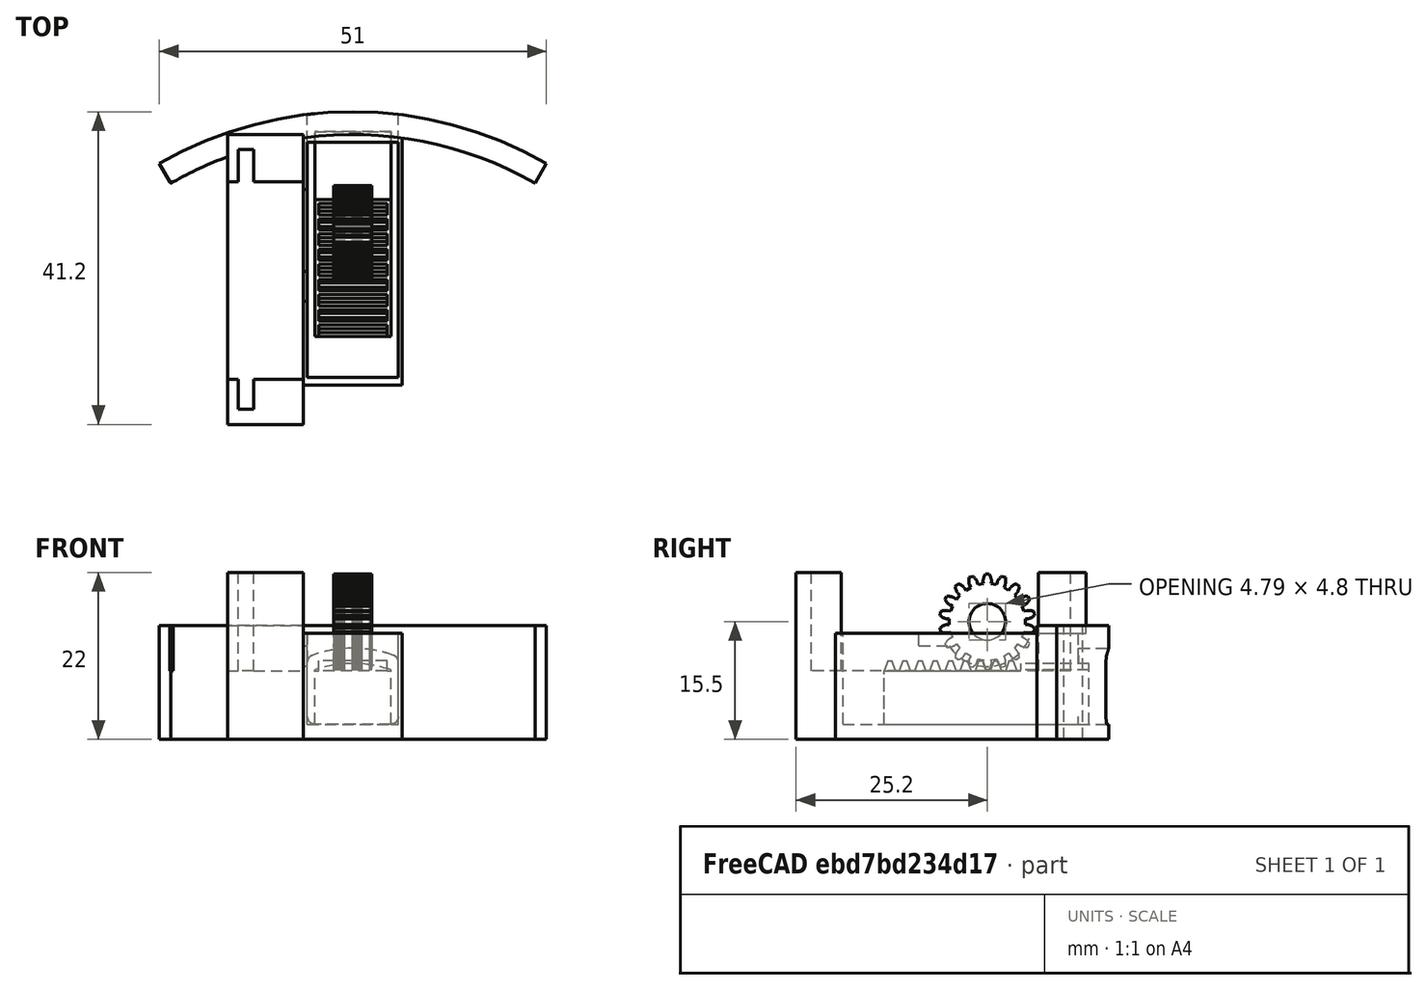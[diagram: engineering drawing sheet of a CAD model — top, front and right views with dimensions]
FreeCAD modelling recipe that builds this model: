
FCSTD DOCUMENT  (FreeCAD 0.16R4924 (Git))
Label: interior_servo_bay_v4p14
License: All rights reserved
LicenseURL: http://en.wikipedia.org/wiki/All_rights_reserved
objects: Part::Feature×11, Part::Box×10, Part::MultiFuse×7, Part::Cut×6, Part::Cylinder×4, Part::Extrusion×3, Part::Thickness×1, Mesh::Feature×1, Part::Fuse×1, Part::FeaturePython×1, Part::Prism×1, Part::MultiCommon×1
note: 46 computed .brp shape members not serialized (recipe doc carries the construction recipe); baked Part::Feature solids carry a one-line shape summary decoded from their .brp

FEATURE [Part::Cylinder] Cylinder  label="bottle_wall"
  Angle = 60
  Height = 15
  Placement = pos=(8.5,-7,0) rot=(0,0,1;1.0472rad)
  Radius = 51
FEATURE [Part::Cylinder] Cylinder001  label="bottle_wall001"
  Angle = 60
  Height = 15
  Placement = pos=(8.5,-7,0) rot=(0,0,1;1.0472rad)
  Radius = 48
FEATURE [Part::Cut] Cut  label="bottle_wall_composite"
  Base = -> Cylinder
  Placement = pos=(0,-2,0) rot=(0,0,1;0rad)
  Tool = -> Cylinder001
FEATURE [Part::Feature] Common_cs  label="pin_cs"
  Placement = pos=(3.5,35,2) rot=(0,0,1;0rad)
  shape: bbox 10 x 2e-07 x 8 mm, 0 faces, 0 solids (baked)
FEATURE [Part::Extrusion] Extrude
  Base = -> Common_cs
  Dir = (0,5,0)
  Solid = true
FEATURE [Part::Thickness] Thickness
  Faces = -> Extrude [Face7]
  Intersection = false
  Join = 0
  Mode = 0
  SelfIntersection = false
  Value = 1
FEATURE [Part::Feature] Common_cs001  label="pin_cs001"
  Placement = pos=(3.5,35,2) rot=(0,0,1;0rad)
  shape: bbox 10 x 2e-07 x 8 mm, 0 faces, 0 solids (baked)
FEATURE [Part::Extrusion] Extrude001
  Base = -> Common_cs001
  Dir = (0,5,0)
  Solid = true
FEATURE [Part::MultiFuse] Fusion  label="bolt_bottle_side_opening"
  Placement = pos=(0,-7,1) rot=(0,0,1;0rad)
  Shapes = -> [Thickness,Extrude,Extrude001]
FEATURE [Part::Box] Box  label="pullBay"
  Height = 15
  Length = 12
  Placement = pos=(2.5,7,2) rot=(0,0,1;0rad)
  Width = 31
FEATURE [Part::Box] Box001  label="Case"
  Height = 14
  Length = 13
  Placement = pos=(2,6,0) rot=(0,0,1;0rad)
  Width = 34
FEATURE [Part::Cut] Cut001  label="cut bay from case"
  Base = -> Box001
  Tool = -> Box
FEATURE [Part::MultiFuse] Fusion001  label="wall plus case"
  Shapes = -> [Cut,Cut001]
FEATURE [Part::Cut] Cut002  label="hole cut out of case"
  Base = -> Fusion001
  Tool = -> Fusion
FEATURE [Mesh::Feature] Mesh  label="servo_motor_2"
  Placement = pos=(33.6,-52,22) rot=(0,0,-1;1.5708rad)
FEATURE [Part::Fuse] union  label="pinion"
FEATURE [Part::FeaturePython] RefineLinearExtrude  # WARN: FeaturePython — macro-defined, semantics opaque (R4)
  Base = -> union
FEATURE [Part::Extrusion] LinearExtrude
  Base = -> RefineLinearExtrude
  Dir = (0,0,5)
  Solid = true
FEATURE [Part::Prism] prism
  Circumradius = 2.4
  Height = 7
  Placement = pos=(0,0,-1) rot=(0,0,1;0rad)
  Polygon = 50
FEATURE [Part::Cut] difference  label="pinion_final"
  Base = -> LinearExtrude
  Placement = pos=(6,26,15.5) rot=(0,1,0;1.5708rad)
  Tool = -> prism
FEATURE [Part::Cylinder] Cylinder002  label="rounded_top"
  Angle = 360
  Height = 40
  Placement = pos=(5,35,-7) rot=(1,0,0;1.5708rad)
  Radius = 15
FEATURE [Part::Box] Box005  label="pin"
  Height = 8
  Length = 10
  Width = 27
FEATURE [Part::MultiCommon] Common  label="rounded pin"
  Shapes = -> [Cylinder002,Box005]
FEATURE [Part::Box] Box006  label="flat_top"
  Height = 10
  Length = 10
  Placement = pos=(0,0,7) rot=(0,0,1;0rad)
  Width = 18
FEATURE [Part::Cut] Cut005
  Base = -> Common
  Placement = pos=(0,11,0) rot=(0,0,1;0rad)
  Tool = -> Box006
FEATURE [Part::Box] cube
  Height = 5
  Length = 18
  Placement = pos=(-12,-4.5,-2.5) rot=(0,0,1;0rad)
  Width = 9
FEATURE [Part::Feature] polyhedron
  Placement = pos=(-11.2451,0,2.5) rot=(0,0,1;0rad)
  shape: bbox 1.51 x 9 x 1.337 mm, 6 faces (baked)
FEATURE [Part::Feature] polyhedron001
  Placement = pos=(-9.24512,0,2.5) rot=(0,0,1;0rad)
  shape: bbox 1.51 x 9 x 1.337 mm, 6 faces (baked)
FEATURE [Part::Feature] polyhedron002
  Placement = pos=(-7.24512,0,2.5) rot=(0,0,1;0rad)
  shape: bbox 1.51 x 9 x 1.337 mm, 6 faces (baked)
FEATURE [Part::Feature] polyhedron003
  Placement = pos=(-5.24512,0,2.5) rot=(0,0,1;0rad)
  shape: bbox 1.51 x 9 x 1.337 mm, 6 faces (baked)
FEATURE [Part::Feature] polyhedron004
  Placement = pos=(-3.24512,0,2.5) rot=(0,0,1;0rad)
  shape: bbox 1.51 x 9 x 1.337 mm, 6 faces (baked)
FEATURE [Part::Feature] polyhedron005
  Placement = pos=(-1.24512,0,2.5) rot=(0,0,1;0rad)
  shape: bbox 1.51 x 9 x 1.337 mm, 6 faces (baked)
FEATURE [Part::Feature] polyhedron006
  Placement = pos=(0.754882,0,2.5) rot=(0,0,1;0rad)
  shape: bbox 1.51 x 9 x 1.337 mm, 6 faces (baked)
FEATURE [Part::Feature] polyhedron007
  Placement = pos=(2.75488,0,2.5) rot=(0,0,1;0rad)
  shape: bbox 1.51 x 9 x 1.337 mm, 6 faces (baked)
FEATURE [Part::Feature] polyhedron008
  Placement = pos=(4.75488,0,2.5) rot=(0,0,1;0rad)
  shape: bbox 1.51 x 9 x 1.337 mm, 6 faces (baked)
FEATURE [Part::MultiFuse] Fusion003  label="rack"
  Placement = pos=(5,23,4.5) rot=(0,0,1;1.5708rad)
  Shapes = -> [cube,polyhedron002,polyhedron003,polyhedron004,polyhedron005,polyhedron,polyhedron007,polyhedron001,polyhedron006,polyhedron008]
FEATURE [Part::MultiFuse] Fusion004  label="pin_3p2"
  Placement = pos=(3.5,1.4,2) rot=(0,0,1;0rad)
  Shapes = -> [Fusion003,Cut005]
FEATURE [Part::Box] Box007  label="mount"
  Height = 22
  Length = 10
  Placement = pos=(-8,2,0) rot=(0,0,1;0rad)
  Width = 37
FEATURE [Part::Box] Box008  label="Cube"
  Height = 13
  Length = 35
  Placement = pos=(-42,1.5,-2) rot=(0,0,1;0rad)
  Width = 2
FEATURE [Part::Box] Box009  label="Cube001"
  Height = 13
  Length = 26
  Placement = pos=(-37.75,-13.6,-2) rot=(0,0,1;0rad)
  Width = 23.7
FEATURE [Part::Box] Box010  label="Cube002"
  Height = 7
  Length = 10
  Placement = pos=(-32,3.3,1.3) rot=(0,0,1;0rad)
  Width = 10
FEATURE [Part::Cylinder] Cylinder003
  Angle = 360
  Height = 6
  Placement = pos=(-31,14.3,4.6) rot=(1,0,0;1.5708rad)
  Radius = 6
FEATURE [Part::MultiFuse] Fusion005  label="simple_servo_rev_eng"
  Placement = pos=(-8.1,-5,11) rot=(0,0,-1;1.5708rad)
  Shapes = -> [Box008,Box010,Cylinder003,Box009]
FEATURE [Part::MultiFuse] Fusion006
  Shapes = -> [Box007,Cut002]
FEATURE [Part::Cut] Cut006
  Base = -> Fusion006
  Tool = -> Fusion005
FEATURE [Part::Box] Box011  label="bracket extention"
  Height = 22
  Length = 10
  Placement = pos=(-8,0.8,0) rot=(0,0,1;0rad)
  Width = 2
FEATURE [Part::MultiFuse] Fusion007
  Shapes = -> [Cut006,Box011]
